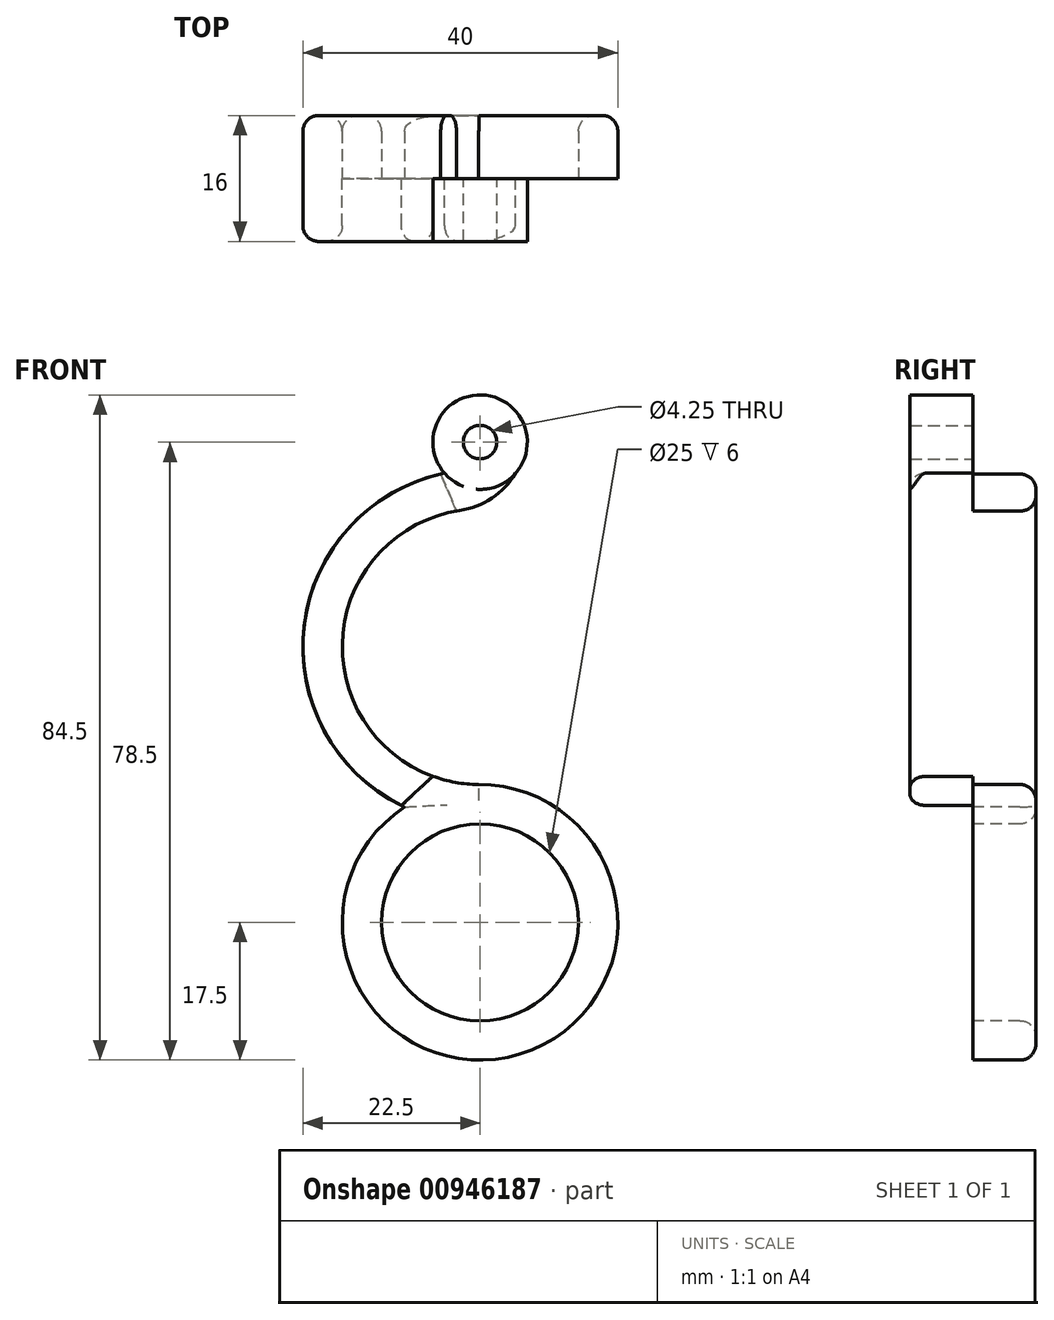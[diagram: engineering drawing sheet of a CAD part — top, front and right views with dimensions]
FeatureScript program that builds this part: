
annotation { "Feature Type Name" : "Feature", "Feature Type Description" : "" }
export const myFeature = defineFeature(function(context is Context, id is Id, definition is map)
    precondition{}
    {
        {
            var Q0;
            Q0=qCreatedBy(makeId("Front.planeOp"),FACE);
            var sketch = newSketch(context, id + "F0", { "sketchPlane" : qUnion([Q0])});
            skArc(sketch, "E0", {"start": v(-6, -16.44) * mm, "mid": v(-17.03, 4.03) * mm, "end": v(2, 17.39) * mm});
            skArc(sketch, "E1.0", {"start": v(-10, -20.16) * mm, "mid": v(-21.28, 7.32) * mm, "end": v(4.51, 22.04) * mm});
            skLineSegment(sketch, "E2", {"start": v(4.51, 22.04) * mm, "end": v(2, 17.39) * mm});
            skLineSegment(sketch, "E3", {"start": v(-6, -16.44) * mm, "end": v(-10, -20.16) * mm});
            skArc(sketch, "E4", {"start": v(4.51, 22.04) * mm, "mid": v(0, 32) * mm, "end": v(-4.51, 22.04) * mm});
            skCircle(sketch, "E5", {"center": v(0, 26) * mm, "radius": 2.12 * mm});
            skSolve(sketch);
        }
        {
            var Q0;
            Q0 = qSketchRegion(id + "F0", true);
            extrude(context, id + "F1", {"entities" : qUnion([Q0]), "depth" : 8 * mm, "offsetDistance" : 25 * mm});
        }
        {
            var Q0;
            Q0=makeQuery(id+"F1.opExtrude","CAP_FACE",FACE,{"disambiguationData":[OSD([sQuery(id+"F0.wireOp",EDGE,"E0"),sQuery(id+"F0.wireOp",EDGE,"E1.0"),sQuery(id+"F0.wireOp",EDGE,"E2"),sQuery(id+"F0.wireOp",EDGE,"E3"),sQuery(id+"F0.wireOp",EDGE,"E4"),sQuery(id+"F0.wireOp",EDGE,"E5")])],"isStart":true});
            var sketch = newSketch(context, id + "F2", { "sketchPlane" : qUnion([Q0])});
            skArc(sketch, "E6", {"start": v(5, 21.94) * mm, "mid": v(22.37, -2.42) * mm, "end": v(0.2, -22.5) * mm});
            skArc(sketch, "E7.0", {"start": v(3, 17.24) * mm, "mid": v(17.44, -1.4) * mm, "end": v(0.2, -17.5) * mm});
            skLineSegment(sketch, "E8", {"start": v(5, 21.94) * mm, "end": v(3, 17.24) * mm});
            skLineSegment(sketch, "E9", {"start": v(0.2, -17.5) * mm, "end": v(0.2, -22.5) * mm});
            skSolve(sketch);
        }
        {
            var Q0;
            Q0 = qSketchRegion(id + "F2", true);
            extrude(context, id + "F3", {"entities" : qUnion([Q0]), "operationType" : NewBodyOperationType.ADD, "depth" : 8 * mm, "offsetDistance" : 25 * mm});
        }
        {
            var Q0;
            Q0=qCreatedBy(makeId("Front.planeOp"),FACE);
            var sketch = newSketch(context, id + "F4", { "sketchPlane" : qUnion([Q0])});
            skPoint(sketch, "E10", {"position": v(0, -22.5) * mm});
            skCircle(sketch, "E11", {"center": v(0, -35) * mm, "radius": 12.5 * mm});
            skCircle(sketch, "E12.0", {"center": v(0, -35) * mm, "radius": 17.5 * mm});
            skSolve(sketch);
        }
        {
            var Q0;
            Q0 = qSketchRegion(id + "F4", true);
            extrude(context, id + "F5", {"entities" : qUnion([Q0]), "operationType" : NewBodyOperationType.ADD, "oppositeDirection" : true, "depth" : 8 * mm, "offsetDistance" : 25 * mm});
        }
        {
            var Q0;
            Q0=makeQuery(id+"F1.opExtrude","SWEPT_EDGE",EDGE,{"disambiguationData":[OSD([sQuery(id+"F0.wireOp",EDGE,"E0"),sQuery(id+"F0.wireOp",EDGE,"E2")])]});
            fillet(context, id + "F6", {"entities" : qUnion([Q0]), "radius" : 10 * mm, "tangentPropagation" : true, "allowEdgeOverflow" : false});
        }
        {
            var Q0;
            Q0=makeQuery(id+"F1.opExtrude","CAP_EDGE",EDGE,{"disambiguationData":[OSD([sQuery(id+"F0.wireOp",EDGE,"E0")])],"isStart":false});
            var Q1;
            Q1=makeQuery(id+"F1.opExtrude","CAP_EDGE",EDGE,{"disambiguationData":[OSD([sQuery(id+"F0.wireOp",EDGE,"E1.0")])],"isStart":false});
            var Q2;
            Q2=makeQuery(id+"F3.opExtrude","CAP_EDGE",EDGE,{"disambiguationData":[OSD([sQuery(id+"F2.wireOp",EDGE,"E6")])],"isStart":false});
            var Q3;
            Q3=makeQuery(id+"F3.opExtrude","CAP_EDGE",EDGE,{"disambiguationData":[OSD([sQuery(id+"F2.wireOp",EDGE,"E7.0")])],"isStart":false});
            var Q4;
            Q4=makeQuery(id+"F5.opExtrude","CAP_EDGE",EDGE,{"disambiguationData":[OSD([sQuery(id+"F4.wireOp",EDGE,"E11")])],"isStart":false});
            var Q5;
            Q5=makeQuery(id+"F5.opExtrude","CAP_EDGE",EDGE,{"disambiguationData":[OSD([sQuery(id+"F4.wireOp",EDGE,"E12.0")])],"isStart":false});
            fillet(context, id + "F7", {"entities" : qUnion([Q0, Q1, Q2, Q3, Q4, Q5]), "radius" : 2 * mm, "tangentPropagation" : true, "allowEdgeOverflow" : false});
        }
        {
            var Q0;
            Q0=makeQuery(id+"F5.opExtrude","CAP_FACE",FACE,{"disambiguationData":[OSD([sQuery(id+"F4.wireOp",EDGE,"E11"),sQuery(id+"F4.wireOp",EDGE,"E12.0")])],"isStart":true});
            var sketch = newSketch(context, id + "F8", { "sketchPlane" : qUnion([Q0])});
            skCircle(sketch, "E13", {"center": v(0, -35) * mm, "radius": 17.62 * mm});
            skSolve(sketch);
        }
        {
            var Q0;
            Q0 = qSketchRegion(id + "F8", true);
            extrude(context, id + "F9", {"entities" : qUnion([Q0]), "operationType" : NewBodyOperationType.REMOVE, "depth" : 15 * mm, "offsetDistance" : 25 * mm});
        }
        {
            var Q0;
            Q0=makeQuery(id+"F1.opExtrude","CAP_FACE",FACE,{"disambiguationData":[OSD([sQuery(id+"F0.wireOp",EDGE,"E0"),sQuery(id+"F0.wireOp",EDGE,"E1.0"),sQuery(id+"F0.wireOp",EDGE,"E2"),sQuery(id+"F0.wireOp",EDGE,"E3"),sQuery(id+"F0.wireOp",EDGE,"E4"),sQuery(id+"F0.wireOp",EDGE,"E5")])],"isStart":true});
            var sketch = newSketch(context, id + "F10", { "sketchPlane" : qUnion([Q0])});
            skCircle(sketch, "E14", {"center": v(0, 26) * mm, "radius": 6.12 * mm});
            skSolve(sketch);
        }
        {
            var Q0;
            Q0 = qSketchRegion(id + "F10", true);
            extrude(context, id + "F11", {"entities" : qUnion([Q0]), "operationType" : NewBodyOperationType.REMOVE, "depth" : 15 * mm, "offsetDistance" : 25 * mm});
        }
    });
